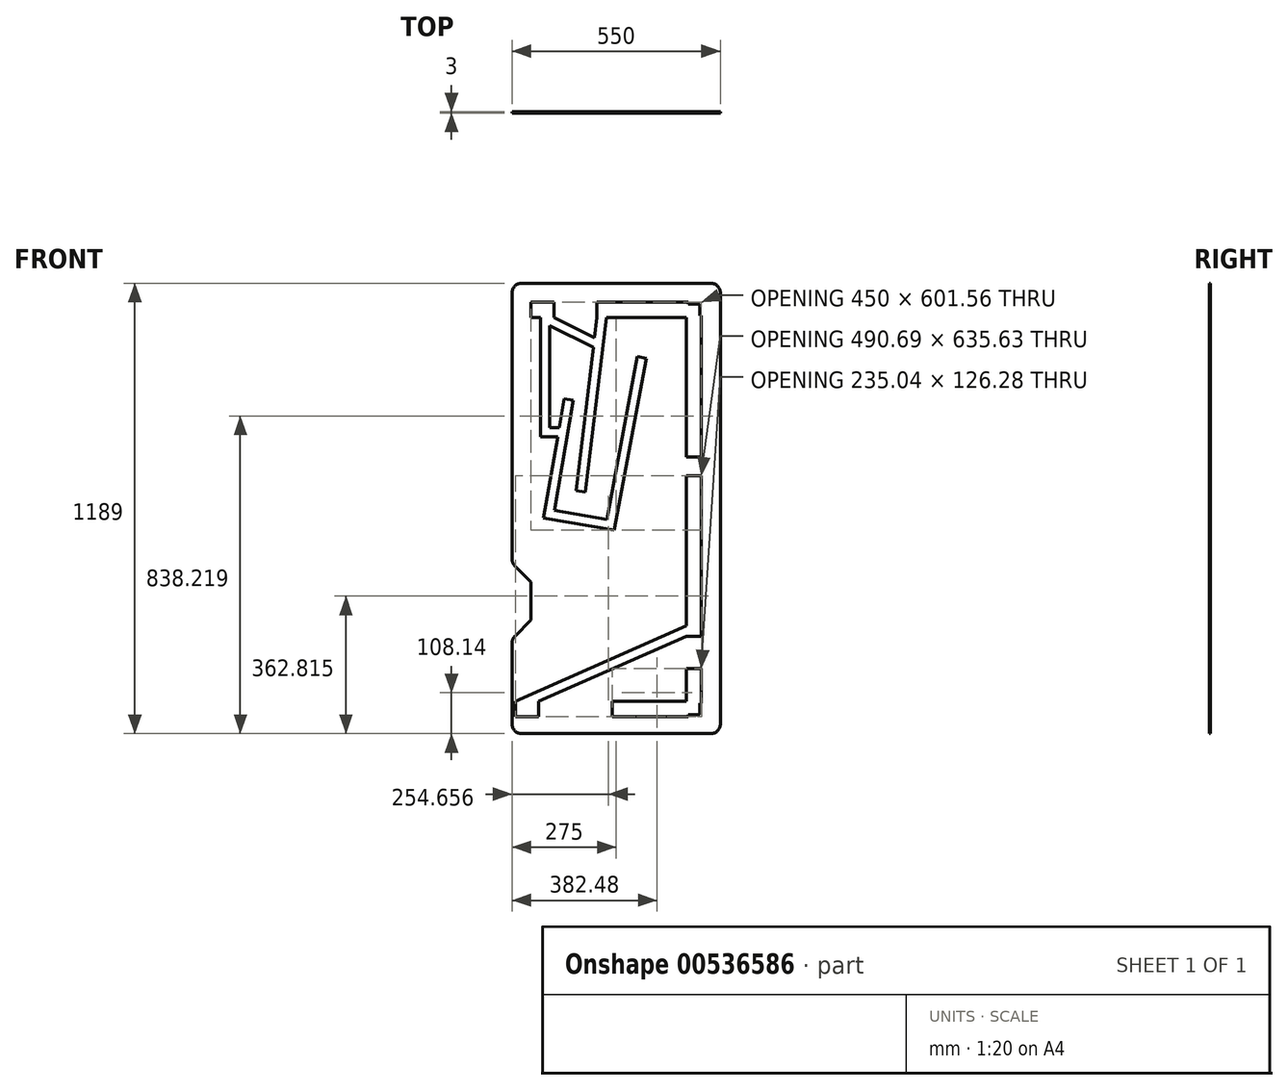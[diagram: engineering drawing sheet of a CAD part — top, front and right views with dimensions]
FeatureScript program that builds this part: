
annotation { "Feature Type Name" : "Feature", "Feature Type Description" : "" }
export const myFeature = defineFeature(function(context is Context, id is Id, definition is map)
    precondition{}
    {
        {
            var Q0;
            Q0=qCreatedBy(makeId("Front.planeOp"),FACE);
            var sketch = newSketch(context, id + "F0", { "sketchPlane" : qUnion([Q0])});
            skLineSegment(sketch, "E0.bottom", {"start": v(222.5, 542) * mm, "end": v(-222.5, 542) * mm});
            skLineSegment(sketch, "E0.top", {"start": v(222.5, -542) * mm, "end": v(-222.5, -542) * mm});
            skLineSegment(sketch, "E0.left", {"start": v(222.5, 542) * mm, "end": v(222.5, -542) * mm});
            skLineSegment(sketch, "E0.right", {"start": v(-222.5, 542) * mm, "end": v(-222.5, -542) * mm});
            skPoint(sketch, "E0.middle", {"position": v(0, 0) * mm});
            skSolve(sketch);
        }
        {
            var Q0;
            Q0 = qSketchRegion(id + "F0", true);
            extrude(context, id + "F1", {"entities" : qUnion([Q0]), "depth" : 32 * mm, "offsetDistance" : 25.4 * mm});
        }
        {
            var Q0;
            Q0=makeQuery(id+"F1.opExtrude","CAP_FACE",FACE,{"disambiguationData":[OSD([sQuery(id+"F0.wireOp",EDGE,"E0.bottom"),sQuery(id+"F0.wireOp",EDGE,"E0.top"),sQuery(id+"F0.wireOp",EDGE,"E0.left"),sQuery(id+"F0.wireOp",EDGE,"E0.right")])],"isStart":false});
            var sketch = newSketch(context, id + "F2", { "sketchPlane" : qUnion([Q0])});
            skLineSegment(sketch, "E1.bottom", {"start": v(-222.5, 542) * mm, "end": v(222.5, 542) * mm});
            skLineSegment(sketch, "E1.top", {"start": v(-222.5, 510) * mm, "end": v(222.5, 510) * mm});
            skLineSegment(sketch, "E1.left", {"start": v(-222.5, 542) * mm, "end": v(-222.5, 510) * mm});
            skLineSegment(sketch, "E1.right", {"start": v(222.5, 542) * mm, "end": v(222.5, 510) * mm});
            skLineSegment(sketch, "E2.top", {"start": v(-194.5, 195) * mm, "end": v(-176.5, 195) * mm});
            skLineSegment(sketch, "E2.left", {"start": v(-194.5, 510) * mm, "end": v(-194.5, 195) * mm});
            skLineSegment(sketch, "E2.right", {"start": v(-176.5, 510) * mm, "end": v(-176.5, 195) * mm});
            skLineSegment(sketch, "E3", {"start": v(-44.5, 510) * mm, "end": v(-99.5, 52.15) * mm});
            skLineSegment(sketch, "E4", {"start": v(-99.5, 52.15) * mm, "end": v(-81.63, 50) * mm});
            skLineSegment(sketch, "E5", {"start": v(-81.63, 50) * mm, "end": v(-26.37, 510) * mm});
            skLineSegment(sketch, "E6", {"start": v(-26.37, 510) * mm, "end": v(-44.5, 510) * mm});
            skLineSegment(sketch, "E7", {"start": v(-132.24, 288.06) * mm, "end": v(-185.3, -19.68) * mm});
            skLineSegment(sketch, "E8", {"start": v(-185.3, -19.68) * mm, "end": v(-167.56, -22.74) * mm});
            skLineSegment(sketch, "E9", {"start": v(-167.56, -22.74) * mm, "end": v(-114.5, 285) * mm});
            skLineSegment(sketch, "E10", {"start": v(-114.5, 285) * mm, "end": v(-132.24, 288.06) * mm});
            skLineSegment(sketch, "E11", {"start": v(-167.56, -22.74) * mm, "end": v(-22.8, -47.7) * mm});
            skLineSegment(sketch, "E12", {"start": v(-22.8, -47.7) * mm, "end": v(-19.5, -30) * mm});
            skLineSegment(sketch, "E13", {"start": v(-22.8, -47.7) * mm, "end": v(60.5, 400) * mm});
            skLineSegment(sketch, "E14", {"start": v(60.5, 400) * mm, "end": v(78.2, 396.7) * mm});
            skLineSegment(sketch, "E15", {"start": v(78.2, 396.7) * mm, "end": v(-5.05, -50.76) * mm});
            skLineSegment(sketch, "E16", {"start": v(-5.05, -50.76) * mm, "end": v(-22.8, -47.7) * mm});
            skLineSegment(sketch, "E17", {"start": v(-164.5, -5) * mm, "end": v(-19.5, -30) * mm});
            skLineSegment(sketch, "E18", {"start": v(-176.5, 510) * mm, "end": v(-51.84, 448.93) * mm});
            skLineSegment(sketch, "E19", {"start": v(-51.84, 448.93) * mm, "end": v(-54.11, 430) * mm});
            skLineSegment(sketch, "E20", {"start": v(-54.11, 430) * mm, "end": v(-176.5, 489.96) * mm});
            skLineSegment(sketch, "E21", {"start": v(-176.5, 489.96) * mm, "end": v(-176.5, 510) * mm});
            skLineSegment(sketch, "E22.bottom", {"start": v(-222.5, -542) * mm, "end": v(222.5, -542) * mm});
            skLineSegment(sketch, "E22.top", {"start": v(-217.93, -510) * mm, "end": v(222.5, -510) * mm});
            skLineSegment(sketch, "E22.left", {"start": v(-222.5, -542) * mm, "end": v(-222.5, -512.02) * mm});
            skLineSegment(sketch, "E22.right", {"start": v(222.5, -542) * mm, "end": v(222.5, -510) * mm});
            skLineSegment(sketch, "E23.bottom", {"start": v(222.5, -510) * mm, "end": v(190.5, -510) * mm});
            skLineSegment(sketch, "E23.top", {"start": v(222.5, 510) * mm, "end": v(190.5, 510) * mm});
            skLineSegment(sketch, "E23.left", {"start": v(222.5, -510) * mm, "end": v(222.5, 510) * mm});
            skLineSegment(sketch, "E23.right", {"start": v(190.5, -510) * mm, "end": v(190.5, 510) * mm});
            skLineSegment(sketch, "E24", {"start": v(-194.5, 510) * mm, "end": v(-176.5, 510) * mm});
            skLineSegment(sketch, "E25", {"start": v(-176.5, 195) * mm, "end": v(-148.28, 195) * mm});
            skLineSegment(sketch, "E26", {"start": v(-148.28, 195) * mm, "end": v(-145.18, 213) * mm});
            skLineSegment(sketch, "E27", {"start": v(-145.18, 213) * mm, "end": v(-176.5, 213) * mm});
            skLineSegment(sketch, "E28", {"start": v(-176.5, 213) * mm, "end": v(-176.5, 195) * mm});
            skLineSegment(sketch, "E29", {"start": v(190.5, -329.68) * mm, "end": v(-359.72, -572.6) * mm});
            skLineSegment(sketch, "E30", {"start": v(-359.72, -572.6) * mm, "end": v(-367, -556.14) * mm});
            skLineSegment(sketch, "E31", {"start": v(-367, -556.14) * mm, "end": v(190.5, -310) * mm});
            skLineSegment(sketch, "E32", {"start": v(190.5, -310) * mm, "end": v(190.5, -329.68) * mm});
            skPoint(sketch, "E33.orphan", {"position": v(-222.5, -510) * mm});
            skLineSegment(sketch, "E34", {"start": v(-222.5, -512.02) * mm, "end": v(-217.93, -510) * mm});
            skSolve(sketch);
        }
        {
            var Q0;
            {var subQ0=sQuery(id+"F2.wireOp",EDGE,"E14");Q0=makeQuery(id+"F2.imprint","IMPRINT",FACE,{"disambiguationData":[TD([[makeQuery(id+"F2.imprint","IMPRINT",EDGE,{"derivedFrom":subQ0}),-1.0]])]});}
            var Q1;
            Q1=makeQuery(id+"F2.imprint","IMPRINT",FACE,{"disambiguationData":[TD([[makeQuery(id+"F2.imprint","IMPRINT",EDGE,{"derivedFrom":sQuery(id+"F2.wireOp",EDGE,"E22.bottom")}),-1.0]])]});
            var Q2;
            {var subQ1=sQuery(id+"F2.wireOp",EDGE,"E8");Q2=makeQuery(id+"F2.imprint","IMPRINT",FACE,{"disambiguationData":[TD([[makeQuery(id+"F2.imprint","IMPRINT",EDGE,{"derivedFrom":subQ1}),1.0]])]});}
            var Q3;
            {var subQ0=sQuery(id+"F2.wireOp",EDGE,"E11");Q3=makeQuery(id+"F2.imprint","IMPRINT",FACE,{"disambiguationData":[TD([[makeQuery(id+"F2.imprint","IMPRINT",EDGE,{"derivedFrom":subQ0}),1.0]])]});}
            var Q4;
            Q4=makeQuery(id+"F2.imprint","IMPRINT",FACE,{"disambiguationData":[TD([[makeQuery(id+"F2.imprint","IMPRINT",EDGE,{"derivedFrom":sQuery(id+"F2.wireOp",EDGE,"E25")}),1.0]])]});
            var Q5;
            Q5=makeQuery(id+"F2.imprint","IMPRINT",FACE,{"disambiguationData":[TD([[makeQuery(id+"F2.imprint","IMPRINT",EDGE,{"derivedFrom":sQuery(id+"F2.wireOp",EDGE,"E2.top")}),1.0]])]});
            var Q6;
            {var subQ0=sQuery(id+"F2.wireOp",EDGE,"E4");Q6=makeQuery(id+"F2.imprint","IMPRINT",FACE,{"disambiguationData":[TD([[makeQuery(id+"F2.imprint","IMPRINT",EDGE,{"derivedFrom":subQ0}),1.0]])]});}
            var Q7;
            Q7=makeQuery(id+"F2.imprint","IMPRINT",FACE,{"disambiguationData":[TD([[makeQuery(id+"F2.imprint","IMPRINT",EDGE,{"derivedFrom":sQuery(id+"F2.wireOp",EDGE,"E18")}),-1.0]])]});
            var Q8;
            Q8=makeQuery(id+"F2.imprint","IMPRINT",FACE,{"disambiguationData":[TD([[makeQuery(id+"F2.imprint","IMPRINT",EDGE,{"derivedFrom":sQuery(id+"F2.wireOp",EDGE,"E1.bottom")}),1.0]])]});
            var Q9;
            {var subQ1=sQuery(id+"F2.wireOp",EDGE,"E23.bottom");Q9=makeQuery(id+"F2.imprint","IMPRINT",FACE,{"disambiguationData":[TD([[makeQuery(id+"F2.imprint","IMPRINT",EDGE,{"derivedFrom":subQ1}),-1.0]])]});}
            var Q10;
            {var subQ3=sQuery(id+"F2.wireOp",EDGE,"E30");Q10=makeQuery(id+"F2.imprint","IMPRINT",FACE,{"disambiguationData":[TD([[makeQuery(id+"F2.imprint","IMPRINT",EDGE,{"derivedFrom":subQ3}),-1.0]])]});}
            var Q11;
            {var subQ3=sQuery(id+"F2.wireOp",EDGE,"E32");Q11=makeQuery(id+"F2.imprint","IMPRINT",FACE,{"disambiguationData":[TD([[makeQuery(id+"F2.imprint","IMPRINT",EDGE,{"derivedFrom":subQ3}),-1.0]])]});}
            extrude(context, id + "F3", {"entities" : qUnion([Q0, Q1, Q2, Q3, Q4, Q5, Q6, Q7, Q8, Q9, Q10, Q11]), "operationType" : NewBodyOperationType.REMOVE, "oppositeDirection" : true, "depth" : 10 * mm, "offsetDistance" : 25 * mm});
        }
        {
            var Q0;
            {var subQ9=sQuery(id+"F0.wireOp",EDGE,"E0.right");Q0=makeQuery(id+"F3.boolean.opBoolean","SPLIT",FACE,{"disambiguationData":[TD([makeQuery(id+"F1.opExtrude","SWEPT_FACE",FACE,{"disambiguationData":[OSD([subQ9])]})])],"derivedFrom":makeQuery(id+"F1.opExtrude","CAP_FACE",FACE,{"disambiguationData":[OSD([sQuery(id+"F0.wireOp",EDGE,"E0.bottom"),sQuery(id+"F0.wireOp",EDGE,"E0.top"),sQuery(id+"F0.wireOp",EDGE,"E0.left"),subQ9])],"isStart":false})});}
            var sketch = newSketch(context, id + "F4", { "sketchPlane" : qUnion([Q0])});
            skLineSegment(sketch, "E35.0", {"start": v(-162.26, 506.7) * mm, "end": v(-48.22, 506.7) * mm});
            skLineSegment(sketch, "E35.1", {"start": v(-162.26, 506.7) * mm, "end": v(-54.56, 453.94) * mm});
            skLineSegment(sketch, "E35.2", {"start": v(-48.22, 506.7) * mm, "end": v(-54.56, 453.94) * mm});
            skLineSegment(sketch, "E36.0", {"start": v(-222.5, 506.7) * mm, "end": v(-197.8, 506.7) * mm});
            skLineSegment(sketch, "E36.1", {"start": v(-197.8, 506.7) * mm, "end": v(-197.8, 191.7) * mm});
            skLineSegment(sketch, "E36.2", {"start": v(-197.8, 191.7) * mm, "end": v(-152.2, 191.7) * mm});
            skLineSegment(sketch, "E36.3", {"start": v(-152.2, 191.7) * mm, "end": v(-189.1, -22.37) * mm});
            skLineSegment(sketch, "E36.4", {"start": v(-2.4, -54.56) * mm, "end": v(-189.1, -22.37) * mm});
            skLineSegment(sketch, "E36.5", {"start": v(82.04, 399.35) * mm, "end": v(-2.4, -54.56) * mm});
            skLineSegment(sketch, "E36.6", {"start": v(57.86, 403.85) * mm, "end": v(82.04, 399.35) * mm});
            skLineSegment(sketch, "E36.7", {"start": v(-22.15, -26.2) * mm, "end": v(57.86, 403.85) * mm});
            skLineSegment(sketch, "E36.8", {"start": v(-160.69, -2.3) * mm, "end": v(-22.15, -26.2) * mm});
            skLineSegment(sketch, "E36.9", {"start": v(-160.69, -2.3) * mm, "end": v(-110.69, 287.7) * mm});
            skLineSegment(sketch, "E36.10", {"start": v(-110.69, 287.7) * mm, "end": v(-134.93, 291.87) * mm});
            skLineSegment(sketch, "E36.11", {"start": v(-78.75, 46.33) * mm, "end": v(-23.44, 506.7) * mm});
            skLineSegment(sketch, "E36.12", {"start": v(-23.44, 506.7) * mm, "end": v(187.2, 506.7) * mm});
            skLineSegment(sketch, "E36.13", {"start": v(187.2, -307.85) * mm, "end": v(187.2, 506.7) * mm});
            skLineSegment(sketch, "E36.14", {"start": v(-222.5, -488.74) * mm, "end": v(187.2, -307.85) * mm});
            skLineSegment(sketch, "E36.15", {"start": v(-103.17, 49.26) * mm, "end": v(-78.75, 46.33) * mm});
            skLineSegment(sketch, "E36.16", {"start": v(-57.67, 428.07) * mm, "end": v(-103.17, 49.26) * mm});
            skLineSegment(sketch, "E36.17", {"start": v(-57.67, 428.07) * mm, "end": v(-173.2, 484.66) * mm});
            skLineSegment(sketch, "E36.18", {"start": v(-173.2, 484.66) * mm, "end": v(-173.2, 216.3) * mm});
            skLineSegment(sketch, "E36.19", {"start": v(-147.96, 216.3) * mm, "end": v(-173.2, 216.3) * mm});
            skLineSegment(sketch, "E36.20", {"start": v(-134.93, 291.87) * mm, "end": v(-147.96, 216.3) * mm});
            skLineSegment(sketch, "E37.0", {"start": v(187.2, -334.74) * mm, "end": v(-202.28, -506.7) * mm});
            skLineSegment(sketch, "E37.1", {"start": v(187.2, -506.7) * mm, "end": v(187.2, -334.74) * mm});
            skLineSegment(sketch, "E37.2", {"start": v(-202.28, -506.7) * mm, "end": v(187.2, -506.7) * mm});
            skLineSegment(sketch, "E38", {"start": v(-222.5, 506.7) * mm, "end": v(-222.5, 542) * mm});
            skLineSegment(sketch, "E39", {"start": v(-222.5, 542) * mm, "end": v(222.5, 542) * mm});
            skLineSegment(sketch, "E40", {"start": v(222.5, 542) * mm, "end": v(222.5, -542) * mm});
            skLineSegment(sketch, "E41", {"start": v(222.5, -542) * mm, "end": v(-222.5, -542) * mm});
            skLineSegment(sketch, "E42", {"start": v(-222.5, -542) * mm, "end": v(-222.5, -488.74) * mm});
            skSolve(sketch);
        }
        {
            var Q0;
            Q0 = qSketchRegion(id + "F4", true);
            var Q1;
            Q1=makeQuery(id+"F3.boolean.opBoolean","COPY",FACE,{"derivedFrom":makeQuery(id+"F3.opExtrude","CAP_FACE",FACE,{"disambiguationData":[OSD([sQuery(id+"F2.wireOp",EDGE,"E1.bottom"),sQuery(id+"F2.wireOp",EDGE,"E1.top"),sQuery(id+"F2.wireOp",EDGE,"E1.left"),sQuery(id+"F2.wireOp",EDGE,"E1.right"),sQuery(id+"F2.wireOp",EDGE,"E2.top"),sQuery(id+"F2.wireOp",EDGE,"E2.left"),sQuery(id+"F2.wireOp",EDGE,"E2.right"),sQuery(id+"F2.wireOp",EDGE,"E3"),sQuery(id+"F2.wireOp",EDGE,"E4"),sQuery(id+"F2.wireOp",EDGE,"E5"),sQuery(id+"F2.wireOp",EDGE,"E7"),sQuery(id+"F2.wireOp",EDGE,"E8"),sQuery(id+"F2.wireOp",EDGE,"E9"),sQuery(id+"F2.wireOp",EDGE,"E10"),sQuery(id+"F2.wireOp",EDGE,"E11"),sQuery(id+"F2.wireOp",EDGE,"E13"),sQuery(id+"F2.wireOp",EDGE,"E14"),sQuery(id+"F2.wireOp",EDGE,"E15"),sQuery(id+"F2.wireOp",EDGE,"E16"),sQuery(id+"F2.wireOp",EDGE,"E17"),sQuery(id+"F2.wireOp",EDGE,"E18"),sQuery(id+"F2.wireOp",EDGE,"E20"),sQuery(id+"F2.wireOp",EDGE,"E22.bottom"),sQuery(id+"F2.wireOp",EDGE,"E22.top"),sQuery(id+"F2.wireOp",EDGE,"E22.left"),sQuery(id+"F2.wireOp",EDGE,"E22.right"),sQuery(id+"F2.wireOp",EDGE,"E23.left"),sQuery(id+"F2.wireOp",EDGE,"E23.right"),sQuery(id+"F2.wireOp",EDGE,"E25"),sQuery(id+"F2.wireOp",EDGE,"E27"),sQuery(id+"F2.wireOp",EDGE,"E29"),sQuery(id+"F2.wireOp",EDGE,"E30"),sQuery(id+"F2.wireOp",EDGE,"E31")])],"isStart":false})});
            extrude(context, id + "F5", {"entities" : qUnion([Q0]), "operationType" : NewBodyOperationType.REMOVE, "endBound" : BoundingType.UP_TO_SURFACE, "oppositeDirection" : true, "depth" : 25 * mm, "endBoundEntityFace" : qUnion([Q1]), "offsetDistance" : 25 * mm});
        }
        {
            var Q0;
            {var subQ0=sQuery(id+"F2.wireOp",EDGE,"E31");var subQ1=sQuery(id+"F2.wireOp",EDGE,"E30");var subQ2=sQuery(id+"F2.wireOp",EDGE,"E29");var subQ3=sQuery(id+"F2.wireOp",EDGE,"E27");var subQ4=sQuery(id+"F2.wireOp",EDGE,"E25");var subQ5=sQuery(id+"F2.wireOp",EDGE,"E23.right");var subQ6=sQuery(id+"F2.wireOp",EDGE,"E23.left");var subQ7=sQuery(id+"F2.wireOp",EDGE,"E22.right");var subQ8=sQuery(id+"F2.wireOp",EDGE,"E22.left");var subQ9=sQuery(id+"F2.wireOp",EDGE,"E22.top");var subQ10=sQuery(id+"F2.wireOp",EDGE,"E22.bottom");var subQ11=sQuery(id+"F2.wireOp",EDGE,"E20");var subQ12=sQuery(id+"F2.wireOp",EDGE,"E18");var subQ13=sQuery(id+"F2.wireOp",EDGE,"E17");var subQ14=sQuery(id+"F2.wireOp",EDGE,"E16");var subQ15=sQuery(id+"F2.wireOp",EDGE,"E15");var subQ16=sQuery(id+"F2.wireOp",EDGE,"E14");var subQ17=sQuery(id+"F2.wireOp",EDGE,"E13");var subQ18=sQuery(id+"F2.wireOp",EDGE,"E11");var subQ19=sQuery(id+"F2.wireOp",EDGE,"E10");var subQ20=sQuery(id+"F2.wireOp",EDGE,"E9");var subQ21=sQuery(id+"F2.wireOp",EDGE,"E8");var subQ22=sQuery(id+"F2.wireOp",EDGE,"E7");var subQ23=sQuery(id+"F2.wireOp",EDGE,"E5");var subQ24=sQuery(id+"F2.wireOp",EDGE,"E4");var subQ25=sQuery(id+"F2.wireOp",EDGE,"E3");var subQ26=sQuery(id+"F2.wireOp",EDGE,"E2.right");var subQ27=sQuery(id+"F2.wireOp",EDGE,"E2.left");var subQ28=sQuery(id+"F2.wireOp",EDGE,"E2.top");var subQ29=sQuery(id+"F2.wireOp",EDGE,"E1.right");var subQ30=sQuery(id+"F2.wireOp",EDGE,"E1.left");var subQ31=sQuery(id+"F2.wireOp",EDGE,"E1.top");var subQ32=sQuery(id+"F2.wireOp",EDGE,"E1.bottom");Q0=makeQuery(id+"F5.boolean.opBoolean","MERGE",FACE,{"derivedFrom":[makeQuery(id+"F3.boolean.opBoolean","COPY",FACE,{"derivedFrom":makeQuery(id+"F3.opExtrude","CAP_FACE",FACE,{"disambiguationData":[OSD([subQ32,subQ31,subQ30,subQ29,subQ28,subQ27,subQ26,subQ25,subQ24,subQ23,subQ22,subQ21,subQ20,subQ19,subQ18,subQ17,subQ16,subQ15,subQ14,subQ13,subQ12,subQ11,subQ10,subQ9,subQ8,subQ7,subQ6,subQ5,subQ4,subQ3,subQ2,subQ1,subQ0])],"isStart":false})}),makeQuery(id+"F5.opExtrude","CAP_FACE",FACE,{"disambiguationData":[OSD([subQ32,subQ31,subQ30,subQ29,subQ28,subQ27,subQ26,subQ25,subQ24,subQ23,subQ22,subQ21,subQ20,subQ19,subQ18,subQ17,subQ16,subQ15,subQ14,subQ13,subQ12,subQ11,subQ10,subQ9,subQ8,subQ7,subQ6,subQ5,subQ4,subQ3,subQ2,subQ1,subQ0])],"isStart":false})]});}
            var sketch = newSketch(context, id + "F6", { "sketchPlane" : qUnion([Q0])});
            skLineSegment(sketch, "E43", {"start": v(-162.26, 506.7) * mm, "end": v(-162.26, 547) * mm});
            skLineSegment(sketch, "E44", {"start": v(-272.5, -567) * mm, "end": v(-272.5, -352.36) * mm});
            skLineSegment(sketch, "E45", {"start": v(-247.5, 597) * mm, "end": v(252.5, 597) * mm});
            skLineSegment(sketch, "E46", {"start": v(277.5, 572) * mm, "end": v(277.5, -567) * mm});
            skLineSegment(sketch, "E47", {"start": v(-48.22, 547) * mm, "end": v(-48.22, 506.7) * mm});
            skLineSegment(sketch, "E48", {"start": v(-48.22, 506.7) * mm, "end": v(-162.26, 506.7) * mm});
            skLineSegment(sketch, "E49", {"start": v(-222.5, -488.74) * mm, "end": v(-263.19, -506.7) * mm});
            skLineSegment(sketch, "E50", {"start": v(-263.19, -506.7) * mm, "end": v(-263.19, -547) * mm});
            skLineSegment(sketch, "E51", {"start": v(-202.28, -547) * mm, "end": v(-202.28, -506.7) * mm});
            skLineSegment(sketch, "E52", {"start": v(-202.28, -506.7) * mm, "end": v(-7.54, -506.7) * mm});
            skLineSegment(sketch, "E53", {"start": v(-7.54, -506.7) * mm, "end": v(-7.54, -547) * mm});
            skLineSegment(sketch, "E54", {"start": v(-247.5, -592) * mm, "end": v(252.5, -592) * mm});
            skLineSegment(sketch, "E55", {"start": v(187.2, -334.74) * mm, "end": v(227.5, -334.74) * mm});
            skLineSegment(sketch, "E56", {"start": v(187.2, -420.72) * mm, "end": v(227.5, -420.72) * mm});
            skLineSegment(sketch, "E57", {"start": v(187.2, -334.74) * mm, "end": v(187.2, -420.72) * mm});
            skLineSegment(sketch, "E58", {"start": v(-48.22, 547) * mm, "end": v(192.5, 547) * mm});
            skLineSegment(sketch, "E59", {"start": v(192.5, 547) * mm, "end": v(192.5, 542) * mm});
            skLineSegment(sketch, "E60", {"start": v(192.5, 542) * mm, "end": v(222.5, 542) * mm});
            skLineSegment(sketch, "E61", {"start": v(222.5, 542) * mm, "end": v(222.5, 512) * mm});
            skLineSegment(sketch, "E62", {"start": v(222.5, 512) * mm, "end": v(227.5, 512) * mm});
            skLineSegment(sketch, "E63", {"start": v(227.5, 512) * mm, "end": v(227.5, 138.63) * mm});
            skLineSegment(sketch, "E64", {"start": v(227.5, -420.72) * mm, "end": v(227.5, -512) * mm});
            skLineSegment(sketch, "E65", {"start": v(227.5, -512) * mm, "end": v(222.5, -512) * mm});
            skLineSegment(sketch, "E66", {"start": v(222.5, -512) * mm, "end": v(222.5, -542) * mm});
            skLineSegment(sketch, "E67", {"start": v(222.5, -542) * mm, "end": v(192.5, -542) * mm});
            skLineSegment(sketch, "E68", {"start": v(192.5, -542) * mm, "end": v(192.5, -547) * mm});
            skLineSegment(sketch, "E69", {"start": v(192.5, -547) * mm, "end": v(-7.54, -547) * mm});
            skLineSegment(sketch, "E70", {"start": v(-202.28, -547) * mm, "end": v(-263.19, -547) * mm});
            skLineSegment(sketch, "E71", {"start": v(-162.26, 547) * mm, "end": v(-222.5, 547) * mm});
            skLineSegment(sketch, "E72", {"start": v(-222.5, 547) * mm, "end": v(-222.5, -83.55) * mm});
            skLineSegment(sketch, "E73", {"start": v(-265.18, -149.32) * mm, "end": v(-222.5, -192) * mm});
            skLineSegment(sketch, "E74", {"start": v(-222.5, -192) * mm, "end": v(-222.5, -292) * mm});
            skLineSegment(sketch, "E75", {"start": v(-222.5, -292) * mm, "end": v(-265.18, -334.68) * mm});
            skLineSegment(sketch, "E76.trimOffspring", {"start": v(-272.5, -131.64) * mm, "end": v(-272.5, 572) * mm});
            skPoint(sketch, "E77.visualSharp", {"position": v(-272.5, -142) * mm});
            skArc(sketch, "E77.filletArc", {"start": v(-272.5, -131.64) * mm, "mid": v(-270.6, -141.21) * mm, "end": v(-265.18, -149.32) * mm});
            skPoint(sketch, "E78.visualSharp", {"position": v(-272.5, -342) * mm});
            skArc(sketch, "E78.filletArc", {"start": v(-265.18, -334.68) * mm, "mid": v(-270.6, -342.79) * mm, "end": v(-272.5, -352.36) * mm});
            skPoint(sketch, "E79.visualSharp", {"position": v(-272.5, -592) * mm});
            skArc(sketch, "E79.filletArc", {"start": v(-272.5, -567) * mm, "mid": v(-265.18, -584.68) * mm, "end": v(-247.5, -592) * mm});
            skPoint(sketch, "E80.visualSharp", {"position": v(277.5, -592) * mm});
            skArc(sketch, "E80.filletArc", {"start": v(252.5, -592) * mm, "mid": v(270.18, -584.68) * mm, "end": v(277.5, -567) * mm});
            skPoint(sketch, "E81.visualSharp", {"position": v(277.5, 597) * mm});
            skArc(sketch, "E81.filletArc", {"start": v(277.5, 572) * mm, "mid": v(270.18, 589.68) * mm, "end": v(252.5, 597) * mm});
            skPoint(sketch, "E82.visualSharp", {"position": v(-272.5, 597) * mm});
            skArc(sketch, "E82.filletArc", {"start": v(-247.5, 597) * mm, "mid": v(-265.18, 589.68) * mm, "end": v(-272.5, 572) * mm});
            skLineSegment(sketch, "E83", {"start": v(-222.5, -83.55) * mm, "end": v(-146.22, -83.55) * mm});
            skLineSegment(sketch, "E84", {"start": v(-146.22, -83.55) * mm, "end": v(-146.22, -398.06) * mm});
            skLineSegment(sketch, "E85", {"start": v(-146.22, -398.06) * mm, "end": v(-222.5, -398.06) * mm});
            skLineSegment(sketch, "E86.trimOffspring", {"start": v(-222.5, -192) * mm, "end": v(-222.5, -488.74) * mm});
            skLineSegment(sketch, "E87", {"start": v(227.5, 138.63) * mm, "end": v(187.2, 138.63) * mm});
            skLineSegment(sketch, "E88", {"start": v(187.2, 138.63) * mm, "end": v(187.2, 88.63) * mm});
            skLineSegment(sketch, "E89", {"start": v(187.2, 88.63) * mm, "end": v(227.5, 88.63) * mm});
            skLineSegment(sketch, "E90.trimOffspring", {"start": v(227.5, 88.63) * mm, "end": v(227.5, -334.74) * mm});
            skSolve(sketch);
        }
        {
            var Q0;
            Q0 = qSketchRegion(id + "F6", true);
            var Q1;
            Q1=makeQuery(id+"F1.opExtrude","CAP_FACE",FACE,{"disambiguationData":[OSD([sQuery(id+"F0.wireOp",EDGE,"E0.bottom"),sQuery(id+"F0.wireOp",EDGE,"E0.top"),sQuery(id+"F0.wireOp",EDGE,"E0.left"),sQuery(id+"F0.wireOp",EDGE,"E0.right")])],"isStart":true});
            var Q2;
            {var subQ9=sQuery(id+"F0.wireOp",EDGE,"E0.right");Q2=makeQuery(id+"F3.boolean.opBoolean","SPLIT",FACE,{"disambiguationData":[TD([makeQuery(id+"F1.opExtrude","SWEPT_FACE",FACE,{"disambiguationData":[OSD([subQ9])]})])],"derivedFrom":makeQuery(id+"F1.opExtrude","CAP_FACE",FACE,{"disambiguationData":[OSD([sQuery(id+"F0.wireOp",EDGE,"E0.bottom"),sQuery(id+"F0.wireOp",EDGE,"E0.top"),sQuery(id+"F0.wireOp",EDGE,"E0.left"),subQ9])],"isStart":false})});}
            extrude(context, id + "F7", {"entities" : qUnion([Q0]), "operationType" : NewBodyOperationType.ADD, "endBound" : BoundingType.UP_TO_SURFACE, "oppositeDirection" : true, "depth" : 25 * mm, "endBoundEntityFace" : qUnion([Q1]), "offsetDistance" : 25 * mm, "hasSecondDirection" : true, "secondDirectionBound" : BoundingType.UP_TO_SURFACE, "secondDirectionOppositeDirection" : false, "secondDirectionDepth" : 25 * mm, "secondDirectionBoundEntityFace" : qUnion([Q2])});
        }
        {
            var Q0;
            Q0=makeQuery(id+"F7.opExtrude","SWEPT_FACE",FACE,{"disambiguationData":[OSD([sQuery(id+"F6.wireOp",EDGE,"E45")])]});
            var sketch = newSketch(context, id + "F8", { "sketchPlane" : qUnion([Q0])});
            skLineSegment(sketch, "E91.bottom", {"start": v(277.5, 0) * mm, "end": v(-272.5, 0) * mm});
            skLineSegment(sketch, "E91.top", {"start": v(277.5, -29) * mm, "end": v(-272.5, -29) * mm});
            skLineSegment(sketch, "E91.left", {"start": v(277.5, 0) * mm, "end": v(277.5, -29) * mm});
            skLineSegment(sketch, "E91.right", {"start": v(-272.5, 0) * mm, "end": v(-272.5, -29) * mm});
            skSolve(sketch);
        }
        {
            var Q0;
            Q0 = qSketchRegion(id + "F8", true);
            extrude(context, id + "F9", {"entities" : qUnion([Q0]), "operationType" : NewBodyOperationType.REMOVE, "endBound" : BoundingType.THROUGH_ALL, "oppositeDirection" : true, "depth" : 25 * mm, "offsetDistance" : 25 * mm});
        }
    });
